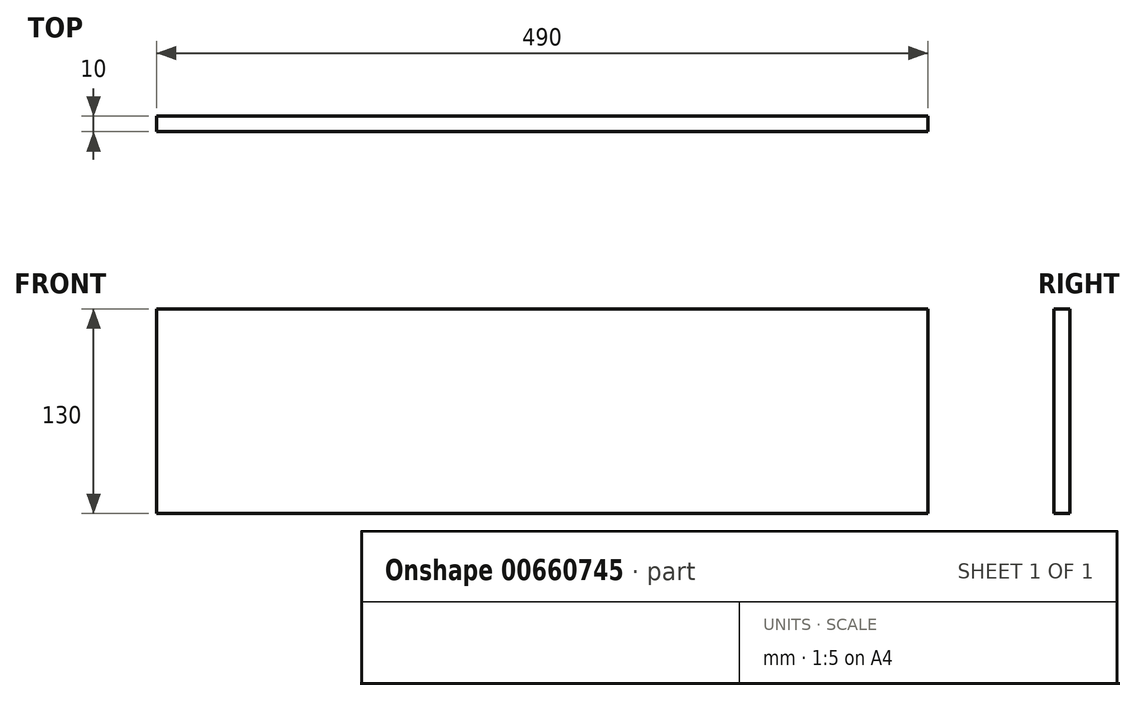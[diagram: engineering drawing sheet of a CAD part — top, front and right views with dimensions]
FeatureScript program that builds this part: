
annotation { "Feature Type Name" : "Feature", "Feature Type Description" : "" }
export const myFeature = defineFeature(function(context is Context, id is Id, definition is map)
    precondition{}
    {
        {
            var Q0;
            Q0=qCreatedBy(makeId("Front.planeOp"),FACE);
            var sketch = newSketch(context, id + "F0", { "sketchPlane" : qUnion([Q0])});
            skLineSegment(sketch, "E0.bottom", {"start": v(0, 0) * mm, "end": v(490, 0) * mm});
            skLineSegment(sketch, "E0.top", {"start": v(0, 130) * mm, "end": v(490, 130) * mm});
            skLineSegment(sketch, "E0.left", {"start": v(0, 0) * mm, "end": v(0, 130) * mm});
            skLineSegment(sketch, "E0.right", {"start": v(490, 0) * mm, "end": v(490, 130) * mm});
            skSolve(sketch);
        }
        {
            var Q0;
            Q0=makeQuery(id+"F0.imprint","IMPRINT",FACE,{"disambiguationData":[TD([[makeQuery(id+"F0.imprint","IMPRINT",EDGE,{"derivedFrom":sQuery(id+"F0.wireOp",EDGE,"E0.bottom")}),1.0]])]});
            extrude(context, id + "F1", {"entities" : qUnion([Q0]), "depth" : 10 * mm, "offsetDistance" : 25 * mm});
        }
    });
